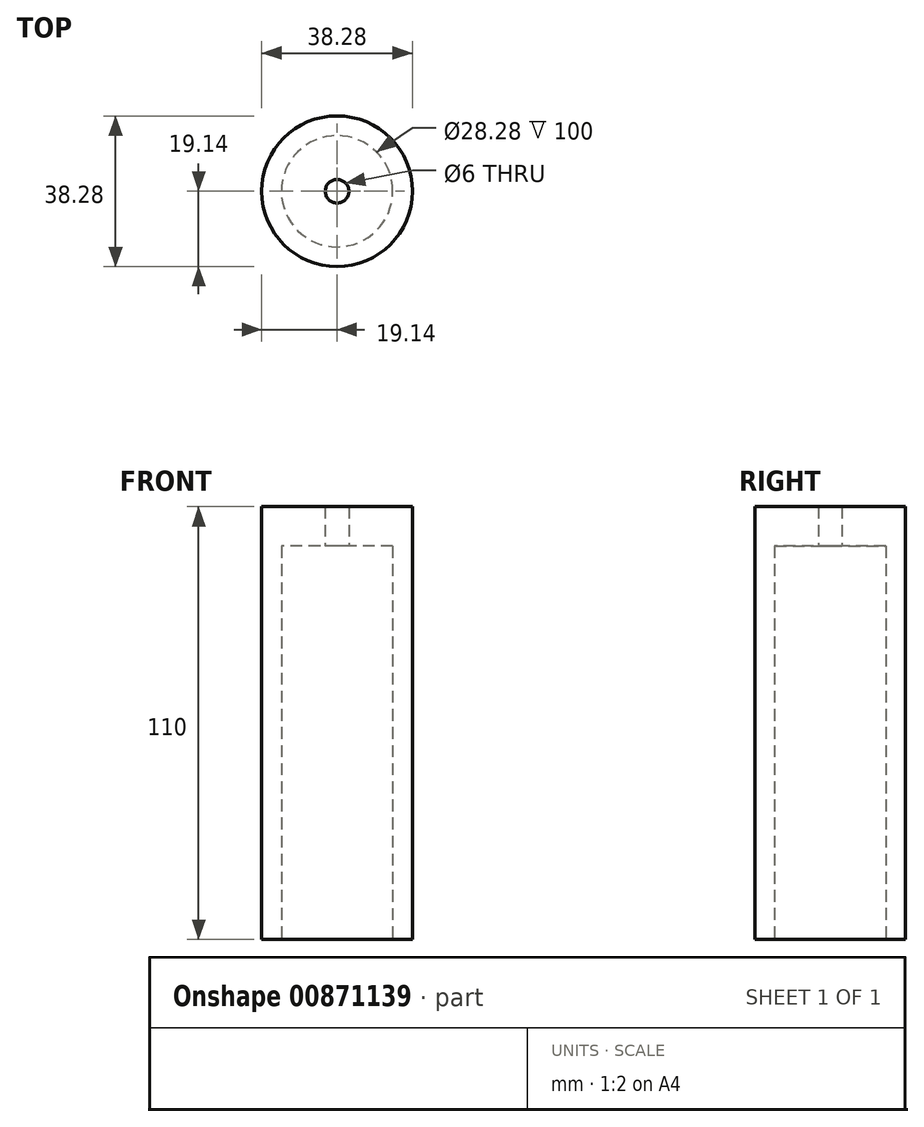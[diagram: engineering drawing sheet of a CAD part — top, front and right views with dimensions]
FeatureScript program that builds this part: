
annotation { "Feature Type Name" : "Feature", "Feature Type Description" : "" }
export const myFeature = defineFeature(function(context is Context, id is Id, definition is map)
    precondition{}
    {
        {
            var Q0;
            Q0=qCreatedBy(makeId("Top.planeOp"),FACE);
            var sketch = newSketch(context, id + "F0", { "sketchPlane" : qUnion([Q0])});
            skCircle(sketch, "E0", {"center": v(0, 0) * mm, "radius": 14.14 * mm});
            skCircle(sketch, "E1", {"center": v(0, 0) * mm, "radius": 19.14 * mm});
            skSolve(sketch);
        }
        {
            var Q0;
            Q0 = qSketchRegion(id + "F0", true);
            var Q1;
            Q1=makeQuery(id+"F0.imprint","IMPRINT",FACE,{"disambiguationData":[TD([[makeQuery(id+"F0.imprint","IMPRINT",EDGE,{"derivedFrom":sQuery(id+"F0.wireOp",EDGE,"E0")}),-1.0]])]});
            extrude(context, id + "F1", {"entities" : qUnion([Q0, Q1]), "depth" : 100 * mm, "offsetDistance" : 25 * mm});
        }
        {
            var Q0;
            Q0=makeQuery(id+"F1.opExtrude","CAP_FACE",FACE,{"disambiguationData":[OSD([sQuery(id+"F0.wireOp",EDGE,"E0"),sQuery(id+"F0.wireOp",EDGE,"E1")])],"isStart":false});
            var sketch = newSketch(context, id + "F2", { "sketchPlane" : qUnion([Q0])});
            skCircle(sketch, "E2", {"center": v(0, 0) * mm, "radius": 19.14 * mm});
            skCircle(sketch, "E3", {"center": v(0, 0) * mm, "radius": 3 * mm});
            skSolve(sketch);
        }
        {
            var Q0;
            Q0 = qSketchRegion(id + "F2", true);
            extrude(context, id + "F3", {"entities" : qUnion([Q0]), "operationType" : NewBodyOperationType.ADD, "depth" : 10 * mm, "offsetDistance" : 25 * mm});
        }
    });
